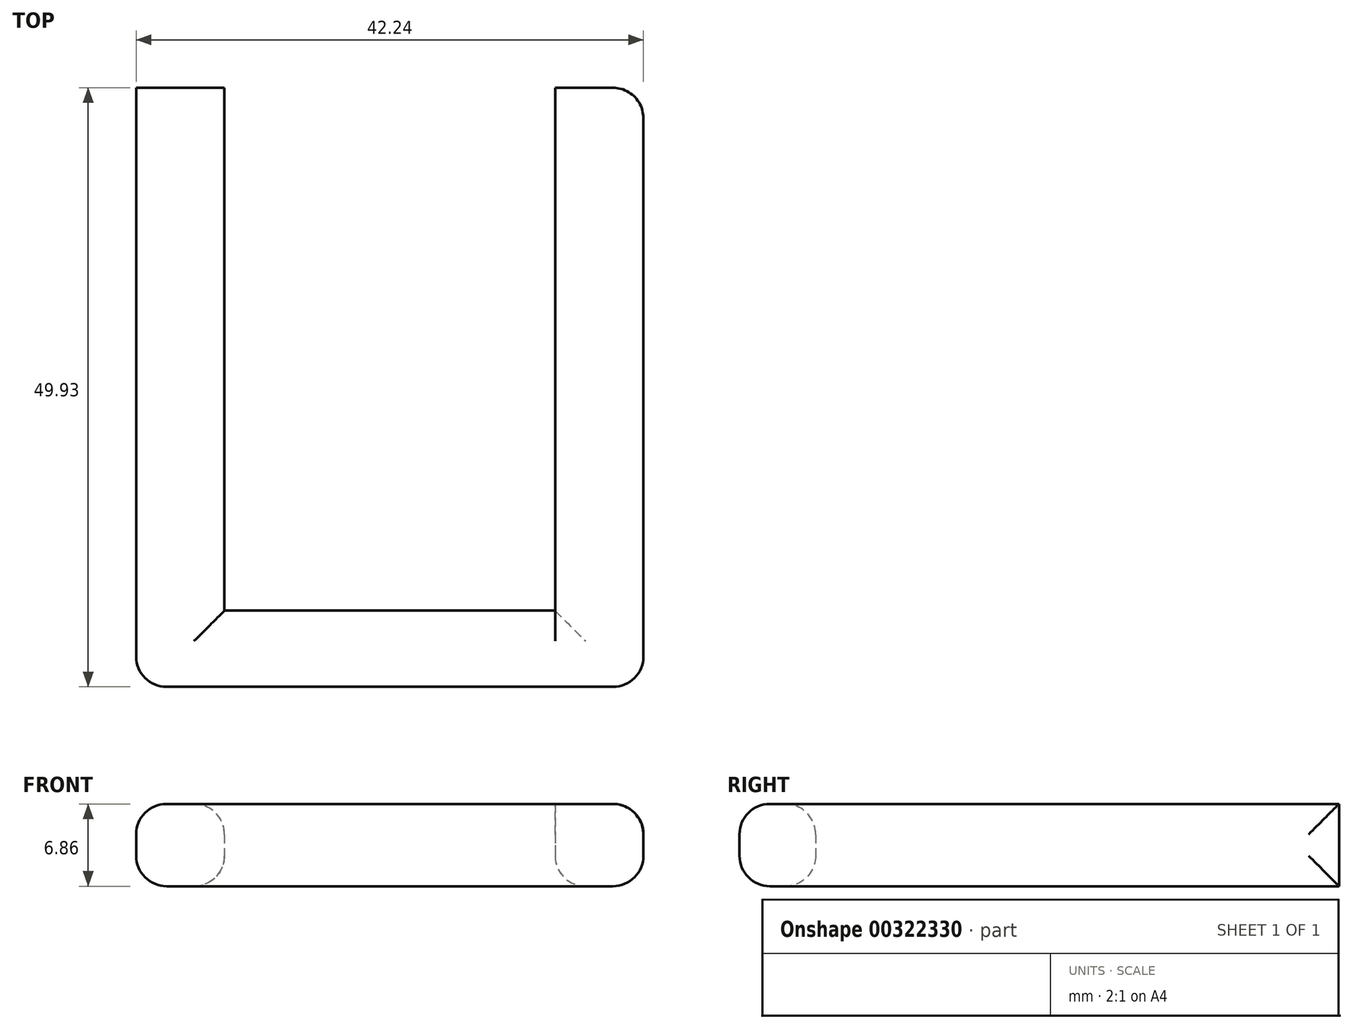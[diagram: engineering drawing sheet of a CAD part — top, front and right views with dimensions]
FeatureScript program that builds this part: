
annotation { "Feature Type Name" : "Feature", "Feature Type Description" : "" }
export const myFeature = defineFeature(function(context is Context, id is Id, definition is map)
    precondition{}
    {
        {
            var Q0;
            Q0=qCreatedBy(makeId("Top.planeOp"),FACE);
            var sketch = newSketch(context, id + "F0", { "sketchPlane" : qUnion([Q0])});
            skLineSegment(sketch, "E0.bottom", {"start": v(0, 0) * mm, "end": v(-21.12, 0) * mm});
            skLineSegment(sketch, "E0.top", {"start": v(-13.77, 49.93) * mm, "end": v(-21.12, 49.93) * mm});
            skLineSegment(sketch, "E0.right", {"start": v(-21.12, 0) * mm, "end": v(-21.12, 49.93) * mm});
            skLineSegment(sketch, "E1", {"start": v(-13.77, 49.93) * mm, "end": v(-13.77, 6.35) * mm});
            skLineSegment(sketch, "E2", {"start": v(-13.77, 6.35) * mm, "end": v(0, 6.35) * mm});
            skPoint(sketch, "E3.orphan", {"position": v(0, 49.93) * mm});
            skLineSegment(sketch, "E4.MirrorCS", {"start": v(0, 0) * mm, "end": v(21.12, 0) * mm});
            skLineSegment(sketch, "E5.MirrorCS", {"start": v(13.77, 49.93) * mm, "end": v(21.12, 49.93) * mm});
            skLineSegment(sketch, "E6.MirrorCS", {"start": v(21.12, 0) * mm, "end": v(21.12, 49.93) * mm});
            skLineSegment(sketch, "E7.MirrorCS", {"start": v(13.77, 49.93) * mm, "end": v(13.77, 6.35) * mm});
            skLineSegment(sketch, "E8.MirrorCS", {"start": v(13.77, 6.35) * mm, "end": v(0, 6.35) * mm});
            skPoint(sketch, "E9.MirrorCS.end.orphan", {"position": v(0, 6.35) * mm});
            skSolve(sketch);
        }
        {
            var Q0;
            Q0=makeQuery(id+"F0.imprint","IMPRINT",FACE,{"disambiguationData":[TD([[makeQuery(id+"F0.imprint","IMPRINT",EDGE,{"derivedFrom":sQuery(id+"F0.wireOp",EDGE,"E0.bottom")}),-1.0]])]});
            extrude(context, id + "F1", {"entities" : qUnion([Q0]), "depth" : 6.86 * mm});
        }
        {
            var Q0;
            Q0=makeQuery(id+"F1.opExtrude","CAP_EDGE",EDGE,{"disambiguationData":[OSD([sQuery(id+"F0.wireOp",EDGE,"E7.MirrorCS")])],"isStart":true});
            var Q1;
            Q1=makeQuery(id+"F1.opExtrude","CAP_EDGE",EDGE,{"disambiguationData":[OSD([sQuery(id+"F0.wireOp",EDGE,"E2"),sQuery(id+"F0.wireOp",EDGE,"E8.MirrorCS")])],"isStart":true});
            var Q2;
            Q2=makeQuery(id+"F1.opExtrude","CAP_EDGE",EDGE,{"disambiguationData":[OSD([sQuery(id+"F0.wireOp",EDGE,"E1")])],"isStart":true});
            var Q3;
            Q3=makeQuery(id+"F1.opExtrude","CAP_EDGE",EDGE,{"disambiguationData":[OSD([sQuery(id+"F0.wireOp",EDGE,"E0.bottom"),sQuery(id+"F0.wireOp",EDGE,"E4.MirrorCS")])],"isStart":false});
            var Q4;
            Q4=makeQuery(id+"F1.opExtrude","SWEPT_EDGE",EDGE,{"disambiguationData":[OSD([sQuery(id+"F0.wireOp",EDGE,"E4.MirrorCS"),sQuery(id+"F0.wireOp",EDGE,"E6.MirrorCS")])]});
            var Q5;
            Q5=makeQuery(id+"F1.opExtrude","SWEPT_EDGE",EDGE,{"disambiguationData":[OSD([sQuery(id+"F0.wireOp",EDGE,"E5.MirrorCS"),sQuery(id+"F0.wireOp",EDGE,"E6.MirrorCS")])]});
            var Q6;
            Q6=makeQuery(id+"F1.opExtrude","CAP_EDGE",EDGE,{"disambiguationData":[OSD([sQuery(id+"F0.wireOp",EDGE,"E6.MirrorCS")])],"isStart":false});
            var Q7;
            Q7=makeQuery(id+"F1.opExtrude","SWEPT_EDGE",EDGE,{"disambiguationData":[OSD([sQuery(id+"F0.wireOp",EDGE,"E0.bottom"),sQuery(id+"F0.wireOp",EDGE,"E0.right")])]});
            var Q8;
            Q8=makeQuery(id+"F1.opExtrude","CAP_EDGE",EDGE,{"disambiguationData":[OSD([sQuery(id+"F0.wireOp",EDGE,"E0.right")])],"isStart":true});
            var Q9;
            Q9=makeQuery(id+"F1.opExtrude","CAP_EDGE",EDGE,{"disambiguationData":[OSD([sQuery(id+"F0.wireOp",EDGE,"E0.right")])],"isStart":false});
            var Q10;
            Q10=makeQuery(id+"F1.opExtrude","CAP_EDGE",EDGE,{"disambiguationData":[OSD([sQuery(id+"F0.wireOp",EDGE,"E0.bottom"),sQuery(id+"F0.wireOp",EDGE,"E4.MirrorCS")])],"isStart":true});
            var Q11;
            Q11=makeQuery(id+"F1.opExtrude","CAP_EDGE",EDGE,{"disambiguationData":[OSD([sQuery(id+"F0.wireOp",EDGE,"E6.MirrorCS")])],"isStart":true});
            var Q12;
            Q12=makeQuery(id+"F1.opExtrude","CAP_EDGE",EDGE,{"disambiguationData":[OSD([sQuery(id+"F0.wireOp",EDGE,"E1")])],"isStart":false});
            var Q13;
            Q13=makeQuery(id+"F1.opExtrude","CAP_EDGE",EDGE,{"disambiguationData":[OSD([sQuery(id+"F0.wireOp",EDGE,"E2"),sQuery(id+"F0.wireOp",EDGE,"E8.MirrorCS")])],"isStart":false});
            fillet(context, id + "F2", {"entities" : qUnion([Q0, Q1, Q2, Q3, Q4, Q5, Q6, Q7, Q8, Q9, Q10, Q11, Q12, Q13]), "radius" : 2.54 * mm, "tangentPropagation" : true, "allowEdgeOverflow" : false});
        }
        {
            var Q0;
            Q0=makeQuery(id+"F1.opExtrude","SWEPT_FACE",FACE,{"disambiguationData":[OSD([sQuery(id+"F0.wireOp",EDGE,"E0.top")])]});
            var sketch = newSketch(context, id + "F3", { "sketchPlane" : qUnion([Q0])});
            skCircle(sketch, "E10", {"center": v(17.64, 3.7) * mm, "radius": 1.72 * mm});
            skSolve(sketch);
        }
        {
            var Q0;
            Q0=makeQuery(id+"F3.imprint","IMPRINT",FACE,{"disambiguationData":[TD([[makeQuery(id+"F3.imprint","IMPRINT",EDGE,{"derivedFrom":sQuery(id+"F3.wireOp",EDGE,"E10")}),1.0]])]});
            extrude(context, id + "F4", {"entities" : qUnion([Q0]), "operationType" : NewBodyOperationType.ADD, "oppositeDirection" : true, "depth" : 13.7 * mm});
        }
    });
